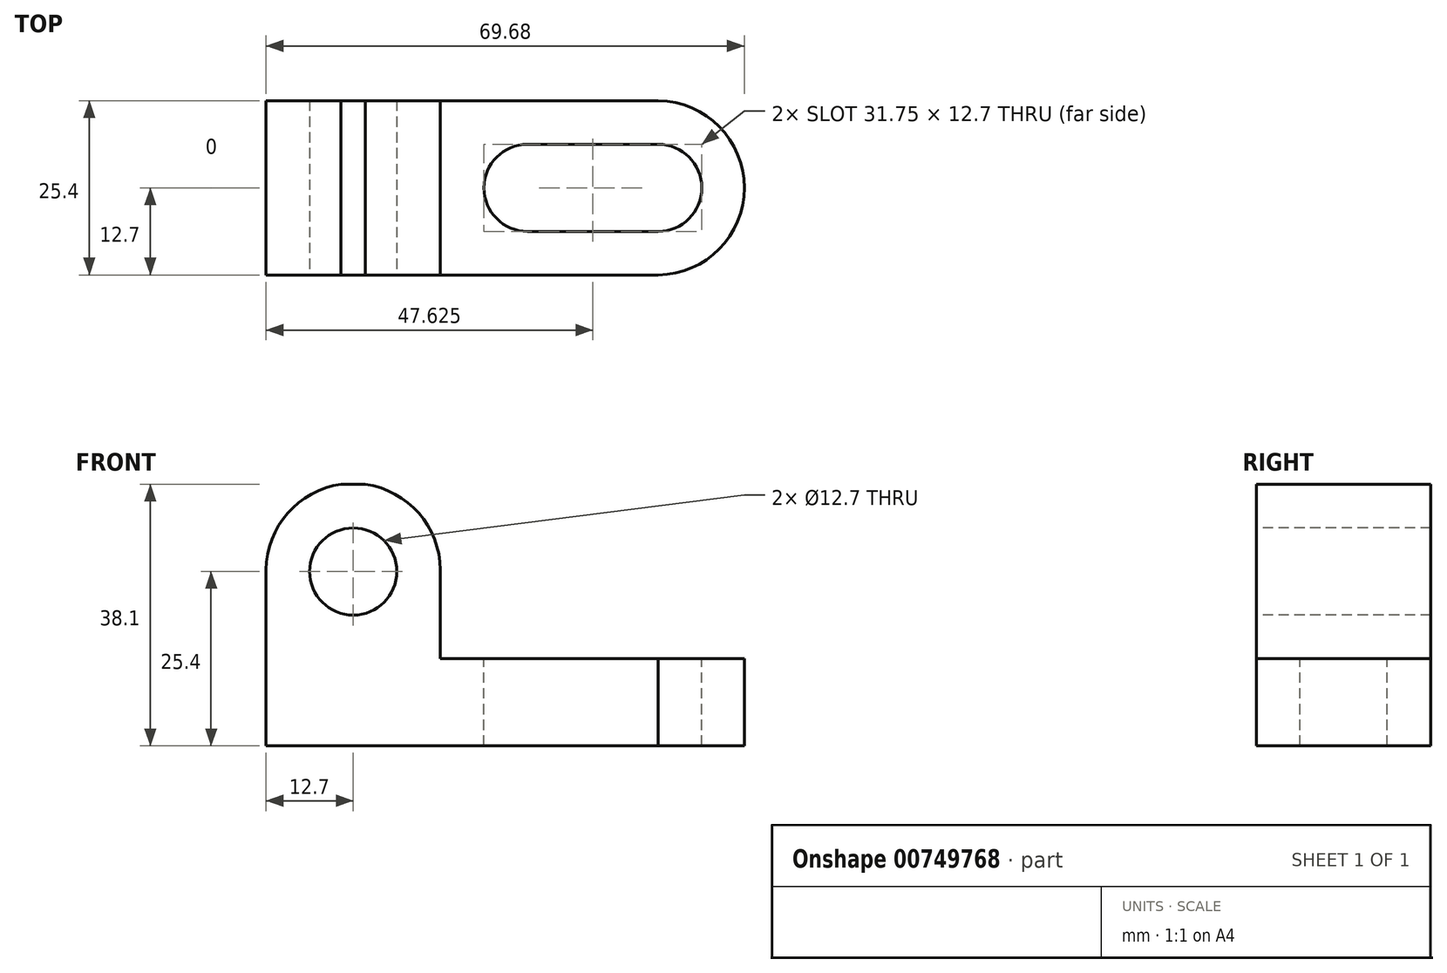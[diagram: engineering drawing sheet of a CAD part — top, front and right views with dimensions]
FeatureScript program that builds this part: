
annotation { "Feature Type Name" : "Feature", "Feature Type Description" : "" }
export const myFeature = defineFeature(function(context is Context, id is Id, definition is map)
    precondition{}
    {
        {
            var Q0;
            Q0=qCreatedBy(makeId("Front.planeOp"),FACE);
            var sketch = newSketch(context, id + "F0", { "sketchPlane" : qUnion([Q0])});
            skLineSegment(sketch, "E0", {"start": v(0, 0) * mm, "end": v(69.85, 0) * mm});
            skLineSegment(sketch, "E1", {"start": v(69.85, 0) * mm, "end": v(69.85, 12.7) * mm});
            skLineSegment(sketch, "E2", {"start": v(69.85, 12.7) * mm, "end": v(25.4, 12.7) * mm});
            skLineSegment(sketch, "E3", {"start": v(25.4, 12.7) * mm, "end": v(25.4, 38.1) * mm});
            skLineSegment(sketch, "E4", {"start": v(25.4, 38.1) * mm, "end": v(0, 38.1) * mm});
            skLineSegment(sketch, "E5", {"start": v(0, 38.1) * mm, "end": v(0, 0) * mm});
            skSolve(sketch);
        }
        {
            var Q0;
            Q0 = qSketchRegion(id + "F0", true);
            extrude(context, id + "F1", {"entities" : qUnion([Q0]), "depth" : 25.4 * mm, "offsetDistance" : 25.4 * mm});
        }
        {
            var Q0;
            Q0=makeQuery(id+"F1.opExtrude","CAP_FACE",FACE,{"disambiguationData":[OSD([sQuery(id+"F0.wireOp",EDGE,"E0"),sQuery(id+"F0.wireOp",EDGE,"E1"),sQuery(id+"F0.wireOp",EDGE,"E2"),sQuery(id+"F0.wireOp",EDGE,"E3"),sQuery(id+"F0.wireOp",EDGE,"E4"),sQuery(id+"F0.wireOp",EDGE,"E5")])],"isStart":false});
            var sketch = newSketch(context, id + "F2", { "sketchPlane" : qUnion([Q0])});
            skLineSegment(sketch, "E6", {"start": v(0, 25.4) * mm, "end": v(25.4, 25.4) * mm});
            skCircle(sketch, "E7", {"center": v(12.7, 25.4) * mm, "radius": 6.35 * mm});
            skArc(sketch, "E8", {"start": v(25.4, 25.4) * mm, "mid": v(12.7, 38.22) * mm, "end": v(0, 25.4) * mm});
            skSolve(sketch);
        }
        {
            var Q0;
            {var subQ0=sQuery(id+"F2.wireOp",EDGE,"E7");var subQ1=sQuery(id+"F2.wireOp",EDGE,"E6");var subQ2=makeQuery(id+"F2.imprint","INTERSECT",VERTEX,{"disambiguationData":[OD(0.0)],"derivedFrom":[subQ1,subQ0]});Q0=makeQuery(id+"F2.imprint","IMPRINT",FACE,{"disambiguationData":[TD([[makeQuery(id+"F2.imprint","IMPRINT",EDGE,{"disambiguationData":[TD([[subQ2,-1.0]])],"derivedFrom":subQ1}),-1.0]])]});}
            var Q1;
            {var subQ0=sQuery(id+"F2.wireOp",EDGE,"E7");var subQ1=sQuery(id+"F2.wireOp",EDGE,"E6");var subQ2=makeQuery(id+"F2.imprint","INTERSECT",VERTEX,{"disambiguationData":[OD(0.0)],"derivedFrom":[subQ1,subQ0]});Q1=makeQuery(id+"F2.imprint","IMPRINT",FACE,{"disambiguationData":[TD([[makeQuery(id+"F2.imprint","IMPRINT",EDGE,{"disambiguationData":[TD([[subQ2,-1.0]])],"derivedFrom":subQ1}),1.0]])]});}
            var Q2;
            {var subQ0=sQuery(id+"F2.wireOp",EDGE,"E8");var subQ1=makeQuery(id+"F1.opExtrude","CAP_EDGE",EDGE,{"disambiguationData":[OSD([sQuery(id+"F0.wireOp",EDGE,"E3")])],"isStart":false});var subQ2=makeQuery(id+"F2.imprint","INTERSECT",VERTEX,{"derivedFrom":[subQ1,subQ0]});Q2=makeQuery(id+"F2.imprint","IMPRINT",FACE,{"disambiguationData":[TD([[makeQuery(id+"F2.imprint","IMPRINT",EDGE,{"disambiguationData":[TD([[subQ2,-1.0]])],"derivedFrom":subQ0}),-1.0]])]});}
            var Q3;
            {var subQ0=sQuery(id+"F2.wireOp",EDGE,"E8");var subQ1=makeQuery(id+"F1.opExtrude","CAP_EDGE",EDGE,{"disambiguationData":[OSD([sQuery(id+"F0.wireOp",EDGE,"E4")])],"isStart":false});var subQ2=makeQuery(id+"F2.imprint","INTERSECT",VERTEX,{"disambiguationData":[OD(1.0)],"derivedFrom":[subQ1,subQ0]});Q3=makeQuery(id+"F2.imprint","IMPRINT",FACE,{"disambiguationData":[TD([[makeQuery(id+"F2.imprint","IMPRINT",EDGE,{"disambiguationData":[TD([[subQ2,-1.0]])],"derivedFrom":subQ0}),-1.0]])]});}
            extrude(context, id + "F3", {"entities" : qUnion([Q0, Q1, Q2, Q3]), "operationType" : NewBodyOperationType.REMOVE, "endBound" : BoundingType.THROUGH_ALL, "oppositeDirection" : true, "depth" : 25.4 * mm, "offsetDistance" : 25.4 * mm});
        }
        {
            var Q0;
            Q0=makeQuery(id+"F1.opExtrude","SWEPT_FACE",FACE,{"disambiguationData":[OSD([sQuery(id+"F0.wireOp",EDGE,"E2")])]});
            var sketch = newSketch(context, id + "F4", { "sketchPlane" : qUnion([Q0])});
            skLineSegment(sketch, "E9", {"start": v(57.15, 0) * mm, "end": v(57.15, -25.4) * mm});
            skLineSegment(sketch, "E10", {"start": v(38.1, 0) * mm, "end": v(38.1, -25.4) * mm});
            skCircle(sketch, "E11", {"center": v(38.1, -12.7) * mm, "radius": 6.35 * mm});
            skCircle(sketch, "E12", {"center": v(57.15, -12.7) * mm, "radius": 6.35 * mm});
            skLineSegment(sketch, "E13", {"start": v(38.1, -6.35) * mm, "end": v(57.15, -6.35) * mm});
            skLineSegment(sketch, "E14", {"start": v(38.1, -19.05) * mm, "end": v(57.15, -19.05) * mm});
            skArc(sketch, "E15", {"start": v(57.15, -25.4) * mm, "mid": v(69.68, -12.7) * mm, "end": v(57.15, 0) * mm});
            skSolve(sketch);
        }
        {
            var Q0;
            {var subQ0=sQuery(id+"F4.wireOp",EDGE,"E11");var subQ1=sQuery(id+"F4.wireOp",EDGE,"E10");var subQ2=makeQuery(id+"F4.imprint","INTERSECT",VERTEX,{"derivedFrom":[subQ1,subQ0,sQuery(id+"F4.wireOp",EDGE,"E13")]});Q0=makeQuery(id+"F4.imprint","IMPRINT",FACE,{"disambiguationData":[TD([[makeQuery(id+"F4.imprint","IMPRINT",EDGE,{"disambiguationData":[TD([[subQ2,-1.0]])],"derivedFrom":subQ1}),-1.0]])]});}
            var Q1;
            {var subQ0=sQuery(id+"F4.wireOp",EDGE,"E11");var subQ1=sQuery(id+"F4.wireOp",EDGE,"E10");var subQ2=makeQuery(id+"F4.imprint","INTERSECT",VERTEX,{"derivedFrom":[subQ1,subQ0,sQuery(id+"F4.wireOp",EDGE,"E13")]});Q1=makeQuery(id+"F4.imprint","IMPRINT",FACE,{"disambiguationData":[TD([[makeQuery(id+"F4.imprint","IMPRINT",EDGE,{"disambiguationData":[TD([[subQ2,-1.0]])],"derivedFrom":subQ1}),1.0]])]});}
            var Q2;
            {var subQ0=sQuery(id+"F4.wireOp",EDGE,"E13");Q2=makeQuery(id+"F4.imprint","IMPRINT",FACE,{"disambiguationData":[TD([[makeQuery(id+"F4.imprint","IMPRINT",EDGE,{"derivedFrom":subQ0}),-1.0]])]});}
            var Q3;
            {var subQ0=sQuery(id+"F4.wireOp",EDGE,"E12");var subQ1=sQuery(id+"F4.wireOp",EDGE,"E9");var subQ2=makeQuery(id+"F4.imprint","INTERSECT",VERTEX,{"derivedFrom":[subQ1,subQ0,sQuery(id+"F4.wireOp",EDGE,"E13")]});Q3=makeQuery(id+"F4.imprint","IMPRINT",FACE,{"disambiguationData":[TD([[makeQuery(id+"F4.imprint","IMPRINT",EDGE,{"disambiguationData":[TD([[subQ2,-1.0]])],"derivedFrom":subQ1}),-1.0]])]});}
            var Q4;
            {var subQ0=sQuery(id+"F4.wireOp",EDGE,"E12");var subQ1=sQuery(id+"F4.wireOp",EDGE,"E9");var subQ2=makeQuery(id+"F4.imprint","INTERSECT",VERTEX,{"derivedFrom":[subQ1,subQ0,sQuery(id+"F4.wireOp",EDGE,"E13")]});Q4=makeQuery(id+"F4.imprint","IMPRINT",FACE,{"disambiguationData":[TD([[makeQuery(id+"F4.imprint","IMPRINT",EDGE,{"disambiguationData":[TD([[subQ2,-1.0]])],"derivedFrom":subQ1}),1.0]])]});}
            var Q5;
            {var subQ0=sQuery(id+"F4.wireOp",EDGE,"E15");Q5=makeQuery(id+"F4.imprint","IMPRINT",FACE,{"disambiguationData":[TD([[makeQuery(id+"F4.imprint","IMPRINT",EDGE,{"derivedFrom":subQ0}),-1.0]])]});}
            extrude(context, id + "F5", {"entities" : qUnion([Q0, Q1, Q2, Q3, Q4, Q5]), "operationType" : NewBodyOperationType.REMOVE, "endBound" : BoundingType.THROUGH_ALL, "oppositeDirection" : true, "depth" : 25.4 * mm, "offsetDistance" : 25.4 * mm});
        }
    });
